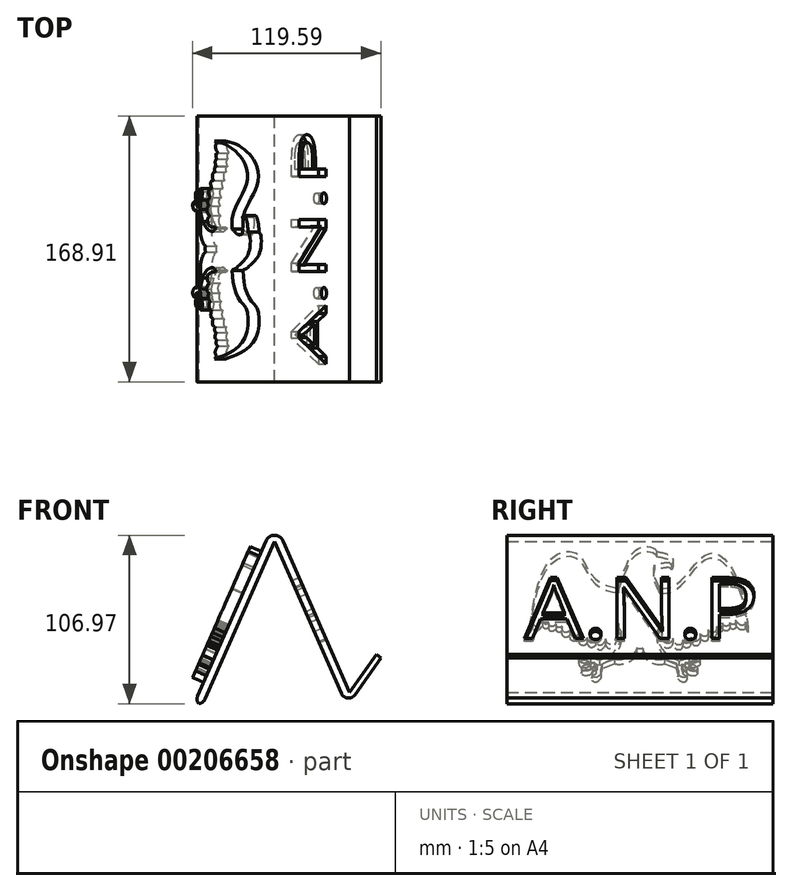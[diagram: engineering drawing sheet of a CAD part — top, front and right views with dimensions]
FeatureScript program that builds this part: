
annotation { "Feature Type Name" : "Feature", "Feature Type Description" : "" }
export const myFeature = defineFeature(function(context is Context, id is Id, definition is map)
    precondition{}
    {
        {
            var Q0;
            Q0=qCreatedBy(makeId("Front.planeOp"),FACE);
            var sketch = newSketch(context, id + "F0", { "sketchPlane" : qUnion([Q0])});
            skLineSegment(sketch, "E0", {"start": v(-46.08, -45.07) * mm, "end": v(0, 59.5) * mm});
            skLineSegment(sketch, "E1", {"start": v(0, 59.5) * mm, "end": v(46.08, -45.07) * mm});
            skLineSegment(sketch, "E2", {"start": v(46.08, -45.07) * mm, "end": v(67.63, -14.35) * mm});
            skLineSegment(sketch, "E3", {"start": v(-46.08, -45.07) * mm, "end": v(-50.76, -43) * mm});
            skLineSegment(sketch, "E4", {"start": v(-50.76, -43) * mm, "end": v(0, 72.2) * mm});
            skLineSegment(sketch, "E5", {"start": v(0, 72.2) * mm, "end": v(47.83, -36.36) * mm});
            skLineSegment(sketch, "E6", {"start": v(47.83, -36.36) * mm, "end": v(64.8, -12.18) * mm});
            skLineSegment(sketch, "E7", {"start": v(64.8, -12.18) * mm, "end": v(67.63, -14.35) * mm});
            skSolve(sketch);
        }
        {
            var Q0;
            Q0=makeQuery(id+"F0.imprint","IMPRINT",FACE,{"disambiguationData":[TD([[makeQuery(id+"F0.imprint","IMPRINT",EDGE,{"derivedFrom":sQuery(id+"F0.wireOp",EDGE,"E0")}),1.0]])]});
            extrude(context, id + "F1", {"entities" : qUnion([Q0]), "depth" : 168.9 * mm});
        }
        {
            var Q0;
            Q0=makeQuery(id+"F1.opExtrude","SWEPT_EDGE",EDGE,{"disambiguationData":[OSD([sQuery(id+"F0.wireOp",EDGE,"E4"),sQuery(id+"F0.wireOp",EDGE,"E5")])]});
            fillet(context, id + "F2", {"entities" : qUnion([Q0]), "radius" : 5.84 * mm, "tangentPropagation" : true, "allowEdgeOverflow" : false});
        }
        {
            var Q0;
            Q0=makeQuery(id+"F1.opExtrude","SWEPT_EDGE",EDGE,{"disambiguationData":[OSD([sQuery(id+"F0.wireOp",EDGE,"E1"),sQuery(id+"F0.wireOp",EDGE,"E2")])]});
            var Q1;
            Q1=makeQuery(id+"F1.opExtrude","SWEPT_EDGE",EDGE,{"disambiguationData":[OSD([sQuery(id+"F0.wireOp",EDGE,"E0"),sQuery(id+"F0.wireOp",EDGE,"E3")])]});
            var Q2;
            Q2=makeQuery(id+"F1.opExtrude","SWEPT_EDGE",EDGE,{"disambiguationData":[OSD([sQuery(id+"F0.wireOp",EDGE,"E3"),sQuery(id+"F0.wireOp",EDGE,"E4")])]});
            fillet(context, id + "F3", {"entities" : qUnion([Q0, Q1, Q2]), "radius" : 5.08 * mm, "tangentPropagation" : true, "allowEdgeOverflow" : false});
        }
        {
            var Q0;
            Q0=makeQuery(id+"F1.opExtrude","SWEPT_FACE",FACE,{"disambiguationData":[OSD([sQuery(id+"F0.wireOp",EDGE,"E5")])]});
            var sketch = newSketch(context, id + "F4", { "sketchPlane" : qUnion([Q0])});
            skText(sketch, "E8", { "text": "A.N.P", "fontName": "OpenSans-Regular.ttf"});
            const initialGuessF4  = {"E8": [-0.15775, -0.01495, 1, 0, 0.04249]};
            skSetInitialGuess(sketch, initialGuessF4);
            skSolve(sketch);
        }
        {
            var Q0;
            Q0 = qSketchRegion(id + "F4", true);
            extrude(context, id + "F5", {"entities" : qUnion([Q0]), "operationType" : NewBodyOperationType.REMOVE, "oppositeDirection" : true, "depth" : 25.4 * mm});
        }
        {
            var Q0;
            Q0=makeQuery(id+"F1.opExtrude","SWEPT_FACE",FACE,{"disambiguationData":[OSD([sQuery(id+"F0.wireOp",EDGE,"E4")])]});
            var sketch = newSketch(context, id + "F6", { "sketchPlane" : qUnion([Q0])});
            skFitSpline(sketch, "E9", {"points": [v(71.9, 16.63) * mm, v(68.61, 16.25) * mm, v(61.94, 18.56) * mm, v(56.43, 23.93) * mm, v(50.45, 31.74) * mm, v(44.83, 38.14) * mm, v(39.91, 40.83) * mm, v(35.34, 40.45) * mm, v(30.77, 36.86) * mm, v(26.79, 31.61) * mm, v(23.63, 24.96) * mm, v(20.23, 14.97) * mm, v(17.83, 4.72) * mm, v(15.87, -10.66) * mm], "startDerivative": vector(-58.22, -14.2) * mm, "endDerivative": vector(-16.13, -148.4) * mm});
            skFitSpline(sketch, "E10", {"points": [v(15.87, -10.66) * mm, v(16.81, -8.27) * mm, v(17.52, -6.73) * mm], "startDerivative": vector(1.73, 4.58) * mm, "endDerivative": vector(1.54, 3.23) * mm});
            skFitSpline(sketch, "E11", {"points": [v(17.52, -6.73) * mm, v(17.52, -8.27) * mm, v(19.08, -9.2) * mm, v(21.04, -8.78) * mm, v(22.83, -6.73) * mm, v(23.7, -5.45) * mm], "startDerivative": vector(-1.93, -9.18) * mm, "endDerivative": vector(4.26, 6.45) * mm});
            skFitSpline(sketch, "E12", {"points": [v(23.7, -5.45) * mm, v(23.7, -7.75) * mm, v(25.26, -8.7) * mm, v(27.37, -7.75) * mm], "startDerivative": vector(-1.36, -7.3) * mm, "endDerivative": vector(6.05, 4.1) * mm});
            skFitSpline(sketch, "E13", {"points": [v(27.37, -7.75) * mm, v(28, -9.04) * mm, v(29.4, -9.9) * mm, v(31.36, -9.12) * mm, v(32.14, -7.75) * mm], "startDerivative": vector(2.1, -5.75) * mm, "endDerivative": vector(2.25, 5.97) * mm});
            skFitSpline(sketch, "E14", {"points": [v(32.14, -7.75) * mm, v(32.14, -9.8) * mm, v(33.62, -10.74) * mm, v(35.81, -10.32) * mm], "startDerivative": vector(-1.22, -6.66) * mm, "endDerivative": vector(6.32, 2.2) * mm});
            skFitSpline(sketch, "E15", {"points": [v(35.81, -10.32) * mm, v(35.81, -11.94) * mm, v(36.99, -14) * mm, v(38.7, -14.25) * mm, v(40.35, -13.48) * mm, v(41.05, -12.45) * mm], "startDerivative": vector(-1, -7.85) * mm, "endDerivative": vector(3.28, 6.42) * mm});
            skFitSpline(sketch, "E16", {"points": [v(41.05, -12.45) * mm, v(41.05, -14.29) * mm, v(41.92, -16.66) * mm, v(44.03, -16.85) * mm, v(46.14, -15.18) * mm], "startDerivative": vector(-0.43, -7.52) * mm, "endDerivative": vector(7.16, 7.47) * mm});
            skFitSpline(sketch, "E17", {"points": [v(46.14, -15.18) * mm, v(46.14, -17.04) * mm, v(47.67, -19.92) * mm, v(49.43, -20.18) * mm, v(51.07, -18.96) * mm, v(51.95, -17.3) * mm], "startDerivative": vector(-1.2, -8.95) * mm, "endDerivative": vector(3.82, 9.19) * mm});
            skFitSpline(sketch, "E18", {"points": [v(51.95, -17.3) * mm, v(52.65, -20.3) * mm, v(54.82, -21.78) * mm, v(56.28, -20.82) * mm, v(57.16, -19.48) * mm], "startDerivative": vector(0.76, -10.8) * mm, "endDerivative": vector(3.67, 6.31) * mm});
            skFitSpline(sketch, "E19", {"points": [v(57.16, -19.48) * mm, v(58.16, -22.49) * mm, v(59.62, -23) * mm, v(61.62, -22.36) * mm, v(63.02, -19.48) * mm, v(63.43, -18.26) * mm], "startDerivative": vector(2.9, -15.14) * mm, "endDerivative": vector(2.3, 6.63) * mm});
            skLineSegment(sketch, "E20", {"start": v(70.5, -10.6) * mm, "end": v(71.52, -8.04) * mm});
            skArc(sketch, "E21", {"start": v(71.52, -8.04) * mm, "mid": v(72.24, -10.65) * mm, "end": v(73.36, -13.13) * mm});
            skArc(sketch, "E22", {"start": v(67.28, -29.21) * mm, "mid": v(72.05, -21.82) * mm, "end": v(73.36, -13.13) * mm});
            skFitSpline(sketch, "E23", {"points": [v(67.28, -29.21) * mm, v(67.06, -29.63) * mm, v(67.1, -30.2) * mm], "startDerivative": vector(-0.59, -0.84) * mm, "endDerivative": vector(0.22, -1.15) * mm});
            skLineSegment(sketch, "E24", {"start": v(67.1, -30.2) * mm, "end": v(59.58, -33.87) * mm});
            skLineSegment(sketch, "E25", {"start": v(59.58, -33.87) * mm, "end": v(53.4, -31.96) * mm});
            skFitSpline(sketch, "E26", {"points": [v(53.4, -31.96) * mm, v(52.36, -31.02) * mm, v(50.05, -30.24) * mm, v(47.79, -30.52) * mm, v(46.6, -31.53) * mm, v(46.2, -32.87) * mm, v(47.12, -34.16) * mm, v(49.17, -35.23) * mm, v(50.77, -35.4) * mm, v(52.26, -34.84) * mm], "startDerivative": vector(-8.98, 9.94) * mm, "endDerivative": vector(14.07, 6.8) * mm});
            skLineSegment(sketch, "E27", {"start": v(52.26, -34.84) * mm, "end": v(55.75, -35.29) * mm});
            skLineSegment(sketch, "E28", {"start": v(55.75, -35.29) * mm, "end": v(53.28, -36.13) * mm});
            skFitSpline(sketch, "E29", {"points": [v(53.28, -36.13) * mm, v(52.07, -36.13) * mm, v(50.36, -36.53) * mm, v(49.05, -37.43) * mm, v(48.16, -38.49) * mm, v(48.05, -39.62) * mm, v(49.27, -40.95) * mm, v(51.76, -40.95) * mm, v(53.28, -40.29) * mm, v(54.84, -38.77) * mm], "startDerivative": vector(-12.11, 0.58) * mm, "endDerivative": vector(12.24, 13.48) * mm});
            skLineSegment(sketch, "E30", {"start": v(54.84, -38.77) * mm, "end": v(58.11, -36.25) * mm});
            skLineSegment(sketch, "E31", {"start": v(58.11, -36.25) * mm, "end": v(57.01, -39.68) * mm});
            skPoint(sketch, "E32.4.internal.snap0", {"position": v(56.47, -37.5) * mm});
            skFitSpline(sketch, "E32", {"points": [v(57.01, -39.68) * mm, v(55.75, -40.62) * mm, v(54.66, -42.42) * mm, v(54.9, -44.13) * mm, v(56.47, -45.5) * mm, v(59.52, -43.88) * mm, v(60.23, -41.39) * mm, v(59.92, -40.45) * mm], "startDerivative": vector(-10.14, -6.26) * mm, "endDerivative": vector(-4, 8.07) * mm});
            skLineSegment(sketch, "E33", {"start": v(59.92, -40.45) * mm, "end": v(61.17, -35.65) * mm});
            skLineSegment(sketch, "E34", {"start": v(61.17, -35.65) * mm, "end": v(68.93, -32.9) * mm});
            skArc(sketch, "E35", {"start": v(68.93, -32.9) * mm, "mid": v(77.32, -31.95) * mm, "end": v(82.6, -25.36) * mm});
            skArc(sketch, "E36", {"start": v(82.6, -25.36) * mm, "mid": v(84.53, -25.67) * mm, "end": v(86.46, -25.36) * mm});
            skArc(sketch, "E37", {"start": v(86.46, -25.36) * mm, "mid": v(92.01, -31.9) * mm, "end": v(100.55, -32.81) * mm});
            skArc(sketch, "E38", {"start": v(96.46, -13.14) * mm, "mid": v(97.8, -22.29) * mm, "end": v(103, -29.93) * mm});
            skLineSegment(sketch, "E39", {"start": v(100.55, -32.81) * mm, "end": v(108.55, -36.1) * mm});
            skLineSegment(sketch, "E40", {"start": v(108.55, -36.1) * mm, "end": v(109.55, -40.66) * mm});
            skFitSpline(sketch, "E41", {"points": [v(109.55, -40.66) * mm, v(109.19, -41.67) * mm, v(109.55, -43.16) * mm, v(110.95, -44.78) * mm, v(112.84, -45.5) * mm, v(114.4, -44.52) * mm, v(114.97, -42.85) * mm, v(114.29, -41.1) * mm, v(112.44, -39.52) * mm], "startDerivative": vector(-5.07, -9.85) * mm, "endDerivative": vector(-14.24, 10.14) * mm});
            skLineSegment(sketch, "E42", {"start": v(103, -29.93) * mm, "end": v(110, -33.72) * mm});
            skLineSegment(sketch, "E43", {"start": v(110, -33.72) * mm, "end": v(115.95, -32.02) * mm});
            skFitSpline(sketch, "E44", {"points": [v(115.95, -32.02) * mm, v(117.72, -30.7) * mm, v(119.98, -30.09) * mm, v(122.32, -31.01) * mm, v(123.24, -32.02) * mm, v(122.53, -34.26) * mm, v(120.7, -35.2) * mm, v(118.07, -35.04) * mm, v(117.08, -34.5) * mm], "startDerivative": vector(12.86, 10.8) * mm, "endDerivative": vector(-8.82, 6.5) * mm});
            skLineSegment(sketch, "E45", {"start": v(117.08, -34.5) * mm, "end": v(113.16, -35.04) * mm});
            skLineSegment(sketch, "E46", {"start": v(113.16, -35.04) * mm, "end": v(115.92, -36.36) * mm});
            skLineSegment(sketch, "E47", {"start": v(112.44, -39.52) * mm, "end": v(111.82, -36.67) * mm});
            skLineSegment(sketch, "E48", {"start": v(111.82, -36.67) * mm, "end": v(111.84, -36.52) * mm});
            skLineSegment(sketch, "E49", {"start": v(111.84, -36.52) * mm, "end": v(114.56, -38.54) * mm});
            skPoint(sketch, "E50.6.internal.snap0", {"position": v(113.2, -37.53) * mm});
            skFitSpline(sketch, "E50", {"points": [v(114.56, -38.54) * mm, v(115.31, -39.74) * mm, v(117.01, -40.64) * mm, v(119.05, -40.9) * mm, v(120.94, -40.19) * mm, v(121.43, -39.08) * mm, v(120.75, -37.53) * mm, v(118.7, -36.56) * mm, v(115.92, -36.36) * mm], "startDerivative": vector(5.5, -11.79) * mm, "endDerivative": vector(-18.79, 0.24) * mm});
            skArc(sketch, "E51", {"start": v(96.46, -13.14) * mm, "mid": v(97.69, -10.64) * mm, "end": v(98.05, -7.88) * mm});
            skLineSegment(sketch, "E52", {"start": v(98.05, -7.88) * mm, "end": v(99.1, -10.2) * mm});
            skFitSpline(sketch, "E53", {"points": [v(99.1, -10.2) * mm, v(99.1, -12.74) * mm, v(99.63, -16.95) * mm, v(101.09, -21.16) * mm, v(103.15, -22.4) * mm, v(105.14, -21.37) * mm, v(106.27, -18.83) * mm], "startDerivative": vector(-0.47, -15.73) * mm, "endDerivative": vector(5.26, 17.52) * mm});
            skFitSpline(sketch, "E54", {"points": [v(106.27, -18.83) * mm, v(107.53, -21.74) * mm, v(109.72, -23.26) * mm, v(111.72, -21.81) * mm, v(112.51, -19.85) * mm], "startDerivative": vector(3.49, -10.9) * mm, "endDerivative": vector(2.43, 8.64) * mm});
            skFitSpline(sketch, "E55", {"points": [v(112.51, -19.85) * mm, v(114.04, -21.16) * mm, v(115.57, -21.45) * mm, v(117.1, -19.85) * mm, v(117.96, -17.67) * mm], "startDerivative": vector(5.85, -5.86) * mm, "endDerivative": vector(2.6, 8.11) * mm});
            skFitSpline(sketch, "E56", {"points": [v(117.96, -17.67) * mm, v(119.49, -19.85) * mm, v(121.15, -19.85) * mm, v(122.48, -18.83) * mm, v(123.47, -15.35) * mm], "startDerivative": vector(5.01, -10.31) * mm, "endDerivative": vector(2.4, 12.95) * mm});
            skFitSpline(sketch, "E57", {"points": [v(123.47, -15.35) * mm, v(125.03, -16.64) * mm, v(126.87, -16.86) * mm, v(128.26, -15.85) * mm, v(128.77, -13.67) * mm, v(128.82, -12.66) * mm], "startDerivative": vector(6.69, -6.96) * mm, "endDerivative": vector(0.17, 5.76) * mm});
            skFitSpline(sketch, "E58", {"points": [v(128.82, -12.66) * mm, v(130.36, -14) * mm, v(131.8, -14.23) * mm, v(133.28, -13.33) * mm, v(133.85, -11.54) * mm, v(134, -9.97) * mm], "startDerivative": vector(6.91, -7.28) * mm, "endDerivative": vector(0.64, 7.92) * mm});
            skFitSpline(sketch, "E59", {"points": [v(134, -9.97) * mm, v(135.74, -10.87) * mm, v(137.13, -9.97) * mm, v(137.7, -8.46) * mm], "startDerivative": vector(4.93, -3.86) * mm, "endDerivative": vector(1.13, 4.89) * mm});
            skFitSpline(sketch, "E60", {"points": [v(137.7, -8.46) * mm, v(139.59, -9.97) * mm, v(141.33, -9.97) * mm, v(142.4, -7.5) * mm], "startDerivative": vector(5.18, -5.2) * mm, "endDerivative": vector(2.06, 8.48) * mm});
            skFitSpline(sketch, "E61", {"points": [v(142.4, -7.5) * mm, v(144.31, -8.53) * mm, v(145.56, -7.5) * mm, v(146.23, -6.2) * mm], "startDerivative": vector(5.35, -4.37) * mm, "endDerivative": vector(1.83, 4.16) * mm});
            skFitSpline(sketch, "E62", {"points": [v(146.23, -6.2) * mm, v(148.15, -8.53) * mm, v(150.45, -9.97) * mm, v(152.65, -7.5) * mm], "startDerivative": vector(5.27, -6.87) * mm, "endDerivative": vector(5.93, 10.12) * mm});
            skFitSpline(sketch, "E63", {"points": [v(152.65, -7.5) * mm, v(154.36, -11.13) * mm], "startDerivative": vector(1.71, -3.62) * mm, "endDerivative": vector(1.71, -3.62) * mm});
            skFitSpline(sketch, "E64", {"points": [v(154.36, -11.13) * mm, v(153.12, -2.03) * mm, v(152.65, 1.08) * mm, v(146.23, 27.62) * mm, v(134, 41.52) * mm, v(123.47, 39.94) * mm, v(116.91, 28.57) * mm, v(107.95, 19.4) * mm, v(98.12, 16.56) * mm], "startDerivative": vector(-13.49, 100.05) * mm, "endDerivative": vector(-88.02, -15.17) * mm});
            skFitSpline(sketch, "E65", {"points": [v(71.9, 16.63) * mm, v(73.73, 21.1) * mm, v(75.45, 26.26) * mm, v(75.12, 32.6) * mm], "startDerivative": vector(5.68, 14.1) * mm, "endDerivative": vector(-2.54, 18.23) * mm});
            skFitSpline(sketch, "E66", {"points": [v(98.12, 16.56) * mm, v(96.18, 24.5) * mm, v(91.78, 35.42) * mm, v(88.23, 41.75) * mm, v(81.35, 45.32) * mm, v(75.12, 43.99) * mm, v(73.94, 41.99) * mm], "startDerivative": vector(-8.07, 41.56) * mm, "endDerivative": vector(-7.07, -21.95) * mm});
            skFitSpline(sketch, "E67", {"points": [v(73.94, 41.99) * mm, v(68.9, 40.82) * mm, v(65.35, 39.05) * mm, v(63.41, 36.12) * mm, v(64.27, 32.6) * mm], "startDerivative": vector(-18.6, -3.68) * mm, "endDerivative": vector(6.48, -15.17) * mm});
            skFitSpline(sketch, "E68", {"points": [v(64.27, 32.6) * mm, v(65.67, 34) * mm, v(68.9, 33.89) * mm, v(75.12, 32.6) * mm], "startDerivative": vector(4.8, 7.03) * mm, "endDerivative": vector(14.95, -3.2) * mm});
            skPoint(sketch, "E69", {"position": v(70.5, -10.6) * mm});
            skFitSpline(sketch, "E70", {"points": [v(63.43, -18.26) * mm, v(64.43, -20.43) * mm, v(66.4, -21.93) * mm, v(68.77, -20.97) * mm, v(70.14, -18.26) * mm, v(70.52, -14.43) * mm, v(70.5, -10.6) * mm], "startDerivative": vector(5.27, -14.87) * mm, "endDerivative": vector(-0.44, 20.15) * mm});
            skSolve(sketch);
        }
        {
            var Q0;
            Q0=makeQuery(id+"F6.imprint","IMPRINT",FACE,{"disambiguationData":[TD([[makeQuery(id+"F6.imprint","IMPRINT",EDGE,{"derivedFrom":sQuery(id+"F6.wireOp",EDGE,"E9")}),1.0]])]});
            extrude(context, id + "F7", {"entities" : qUnion([Q0]), "depth" : 7.62 * mm});
        }
    });
